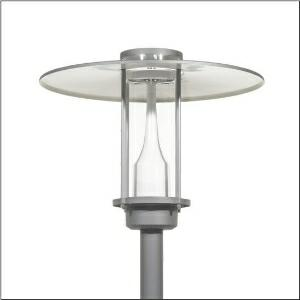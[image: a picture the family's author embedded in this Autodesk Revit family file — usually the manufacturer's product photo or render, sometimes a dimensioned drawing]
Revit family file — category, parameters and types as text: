
# Revit family: city-light_plus_iq___st1_2a_5xa5275mf14h_a6f0
name_source: partatom
category: Lighting Fixtures
units: mm (PartAtom-declared; Revit-internal decimal feet)

## family parameters
Cut with Voids When Loaded = No
Host = Face
Light Source = No
Part Type = Normal
Room Calculation Point = No
Round Connector Dimension = Use Diameter
Shared = No

## types (1)
- --- (1 x LED, 1470 lm, 11.8 W, 2700K)
    Apparent Load = 12 VA
    CIE Flux Codes = 22 62 93 97 100
    Color Rendering = 70
    Color Temperature = 2700K
    Default Elevation = 1800 mm
    Description = City-Light Plus iQ, mast luminaire, Module 540 iQ-SR, primary light control with 3 zone facetted reflector, of plastic, silver coated, highly specular, structured, primary optical cover: cover, of PMMA, transparent, light distribution: ST1.2a, light emission: direct distribution, primary light characteristic: asymmetric, installation type: post-top, LED, High Power LED, rated luminous flux: 1.470lm, luminous efficacy: 125lm/W, light colour: 727, colour temperature: 2700K, control gear: iQ Street-Remote, control: pre-setting: logarithmic dimming characteristic, Street-Remote, Auto-Match, Temp-Guard, Lumen-Switch, Night-Set, Smart-Wire, Light-Fading, Desk-Remote (wireless, voltage-free reading and setting of iQ features in the workshop via application-optimized NFC function/RFID function), optimised constant luminous flux control (CLO 2.0), with terminal, 6-pole, max. 2.5mm², mains connection: 230..240V, AC, 50/60Hz, start of lifetime: 12W, end of service life: 12W, reduction: 6W, luminaire housing, upper part, of glass-fibre reinforced polyester, coated, Siteco® metallic grey (DB 702S), diameter: 750mm, height: 590mm, spigot size: d x l = 76 x 70mm (post-top) | with reducer (optional accessory) 60 x 70mm, mounting height: 3..5m, post-top mast mounting element, of diecast aluminium, coated, Siteco® metallic grey (DB 702S), Module 540 iQ-SR, traffic white (RAL 9016), equipment: standard, protection rating (complete): IP65, insulation class (complete): insulation class II (safety insulation), certification: CE, ENEC, VDE, packaging unit: 1 piece

Light Distribution: ST1.2a
    Height = 590 mm
    Lamp = 1 x LED
    Lamp Light Flux = 1470 lm
    Lamp Power = 11.8 W
    Lamp count = 1
    Length = 750 mm
    Luminous efficacy = 125 lm/W
    Manufacturer = Siteco
    ModVariant = No
    Model = 5XA5275MF14H
    Number of Poles = 1
    OnlyDefault = Yes
    Power Factor = 1
    Product Name = City-Light Plus iQ | ST1.2a
    Product group = mast luminaire | pylon top
    ProductGroupID = 6100
    Protection Class = Protection class II
    Protection Degree = IP 65
    RLX_Detail_Level = 1
    RLX_Emergency_Light_Flux = 0 lm
    RLX_Emergency_Type = 0
    RLX_Emergency_Type_DB = No
    RlxData = <blob elided: 96157 chars, md5=cf1861e2>
    Socket = socket
    Standby Power = 0 W
    System Light Flux = 1470 lm
    System Power = 12 W
    Type Comments = factory setting: luminous flux: 100 % | dim-lin: 254 | 472 mA
    Type Image = l_1006456.jpg
    URL = http://relux.com
    VarID = @adj_178415
    Voltage = 0 V
    Weight = 0.00 kg
    Width = 0 mm  [stored 0 ft]

note: [stored X ft] marks values corroborated as IEEE doubles in the binary element streams (Revit-internal decimal feet)

## geometry (parser evidence)
native form markers: Blend x4, Sweep x10
no freeform markers — native parametric forms only
